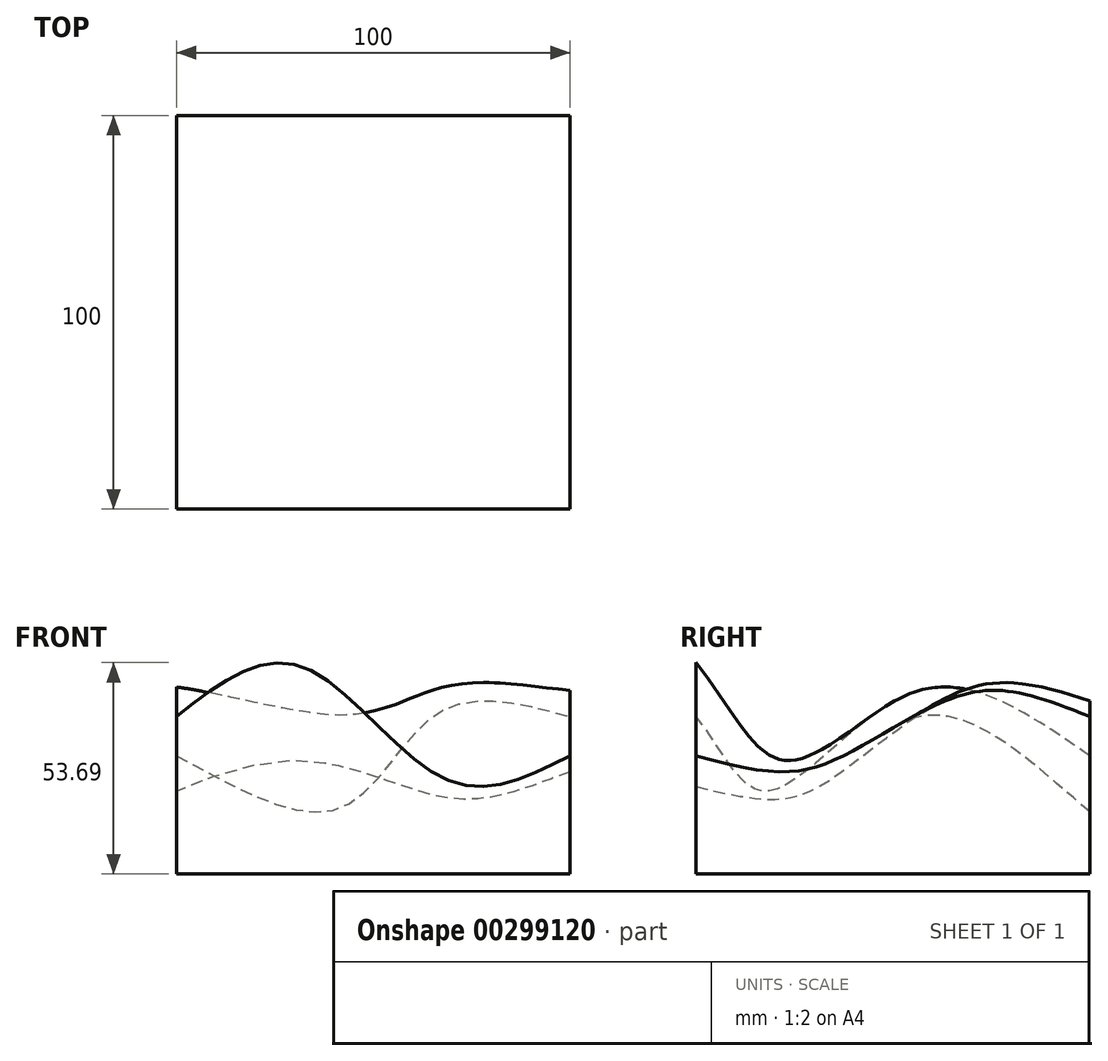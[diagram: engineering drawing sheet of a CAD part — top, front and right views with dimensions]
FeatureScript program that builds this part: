
annotation { "Feature Type Name" : "Feature", "Feature Type Description" : "" }
export const myFeature = defineFeature(function(context is Context, id is Id, definition is map)
    precondition{}
    {
        {
            var Q0;
            Q0=qCreatedBy(makeId("Front.planeOp"),FACE);
            var sketch = newSketch(context, id + "F0", { "sketchPlane" : qUnion([Q0])});
            skLineSegment(sketch, "E0", {"start": v(-50, 0) * mm, "end": v(50, 0) * mm});
            skLineSegment(sketch, "E1", {"start": v(50, 0) * mm, "end": v(50, 40) * mm});
            skLineSegment(sketch, "E2", {"start": v(-50, 0) * mm, "end": v(-50, 30) * mm});
            skFitSpline(sketch, "E3", {"points": [v(-50, 30) * mm, v(-9.21, 16.49) * mm, v(16.58, 40.99) * mm, v(50, 40) * mm], "startDerivative": vector(102.5, -53.01) * mm, "endDerivative": vector(115.32, -30.6) * mm});
            skSolve(sketch);
        }
        {
            var Q0;
            Q0=qCreatedBy(makeId("Front.planeOp"),FACE);
            cPlane(context, id + "F1", {"entities" : qUnion([Q0]), "cplaneType" : CPlaneType.OFFSET, "offset" : 100 * mm, "width" : 150 * mm, "height" : 150 * mm});
        }
        {
            var Q0;
            Q0=qCreatedBy(id+"F1.planeOp",FACE);
            var sketch = newSketch(context, id + "F2", { "sketchPlane" : qUnion([Q0])});
            skLineSegment(sketch, "E4.0", {"start": v(-50, 0) * mm, "end": v(50, 0) * mm});
            skLineSegment(sketch, "E5", {"start": v(50, 0) * mm, "end": v(50, 30) * mm});
            skLineSegment(sketch, "E6", {"start": v(-50, 0) * mm, "end": v(-50, 40) * mm});
            skFitSpline(sketch, "E7", {"points": [v(-50, 40) * mm, v(-18.97, 52.96) * mm, v(18.79, 23.86) * mm, v(50, 30) * mm], "startDerivative": vector(97.7, 76.8) * mm, "endDerivative": vector(101.65, 51.44) * mm});
            skSolve(sketch);
        }
        {
            var Q0;
            Q0=qCreatedBy(makeId("Right.planeOp"),FACE);
            var Q1;
            Q1=sQuery(id+"F0.wireOp",VERTEX,"E3.3.internal");
            cPlane(context, id + "F3", {"entities" : qUnion([Q0, Q1]), "cplaneType" : CPlaneType.PLANE_POINT, "offset" : 25 * mm, "width" : 150 * mm, "height" : 150 * mm});
        }
        {
            var Q0;
            Q0=qCreatedBy(id+"F3.planeOp",FACE);
            var sketch = newSketch(context, id + "F4", { "sketchPlane" : qUnion([Q0])});
            skFitSpline(sketch, "E8", {"points": [v(0, 40) * mm, v(-32.1, 45.55) * mm, v(-63.83, 29.45) * mm, v(-100, 30) * mm], "startDerivative": vector(-132.85, 53.04) * mm, "endDerivative": vector(-170.86, 48.08) * mm});
            skLineSegment(sketch, "E9", {"start": v(-100, 0) * mm, "end": v(0, 0) * mm});
            skSolve(sketch);
        }
        {
            var Q0;
            Q0=qCreatedBy(makeId("Right.planeOp"),FACE);
            var Q1;
            Q1=sQuery(id+"F0.wireOp",VERTEX,"E3.0.internal");
            cPlane(context, id + "F5", {"entities" : qUnion([Q0, Q1]), "cplaneType" : CPlaneType.PLANE_POINT, "offset" : 25 * mm, "width" : 150 * mm, "height" : 150 * mm});
        }
        {
            var Q0;
            Q0=qCreatedBy(id+"F5.planeOp",FACE);
            var sketch = newSketch(context, id + "F6", { "sketchPlane" : qUnion([Q0])});
            skLineSegment(sketch, "E10", {"start": v(0, 0) * mm, "end": v(-100, 0) * mm});
            skFitSpline(sketch, "E11", {"points": [v(0, 30) * mm, v(-44.96, 46.09) * mm, v(-82.2, 21) * mm, v(-100, 40) * mm], "startDerivative": vector(-130.65, 90.01) * mm, "endDerivative": vector(-74.47, 90.57) * mm});
            skSolve(sketch);
        }
        {
            var Q0;
            Q0=makeQuery(id+"F0.imprint","IMPRINT",FACE,{"disambiguationData":[TD([[makeQuery(id+"F0.imprint","IMPRINT",EDGE,{"derivedFrom":sQuery(id+"F0.wireOp",EDGE,"E0")}),1.0]])]});
            var Q1;
            Q1=makeQuery(id+"F2.imprint","IMPRINT",FACE,{"disambiguationData":[TD([[makeQuery(id+"F2.imprint","IMPRINT",EDGE,{"derivedFrom":sQuery(id+"F2.wireOp",EDGE,"E4.0")}),1.0]])]});
            var Q2;
            Q2=sQuery(id+"F6.wireOp",EDGE,"E11");
            var Q3;
            Q3=sQuery(id+"F4.wireOp",EDGE,"E8");
            loft(context, id + "F7", {"addGuides" : true, "sheetProfilesArray" : [{ "sheetProfileEntities" : qUnion([Q0]) }, { "sheetProfileEntities" : qUnion([Q1]) }], "guidesArray" : [{ "guideEntities" : qUnion([Q2]), "guideDerivativeType" : LoftGuideDerivativeType.DEFAULT, "guideDerivativeMagnitude" : 1 }, { "guideEntities" : qUnion([Q3]), "guideDerivativeType" : LoftGuideDerivativeType.DEFAULT, "guideDerivativeMagnitude" : 1 }]});
        }
    });
